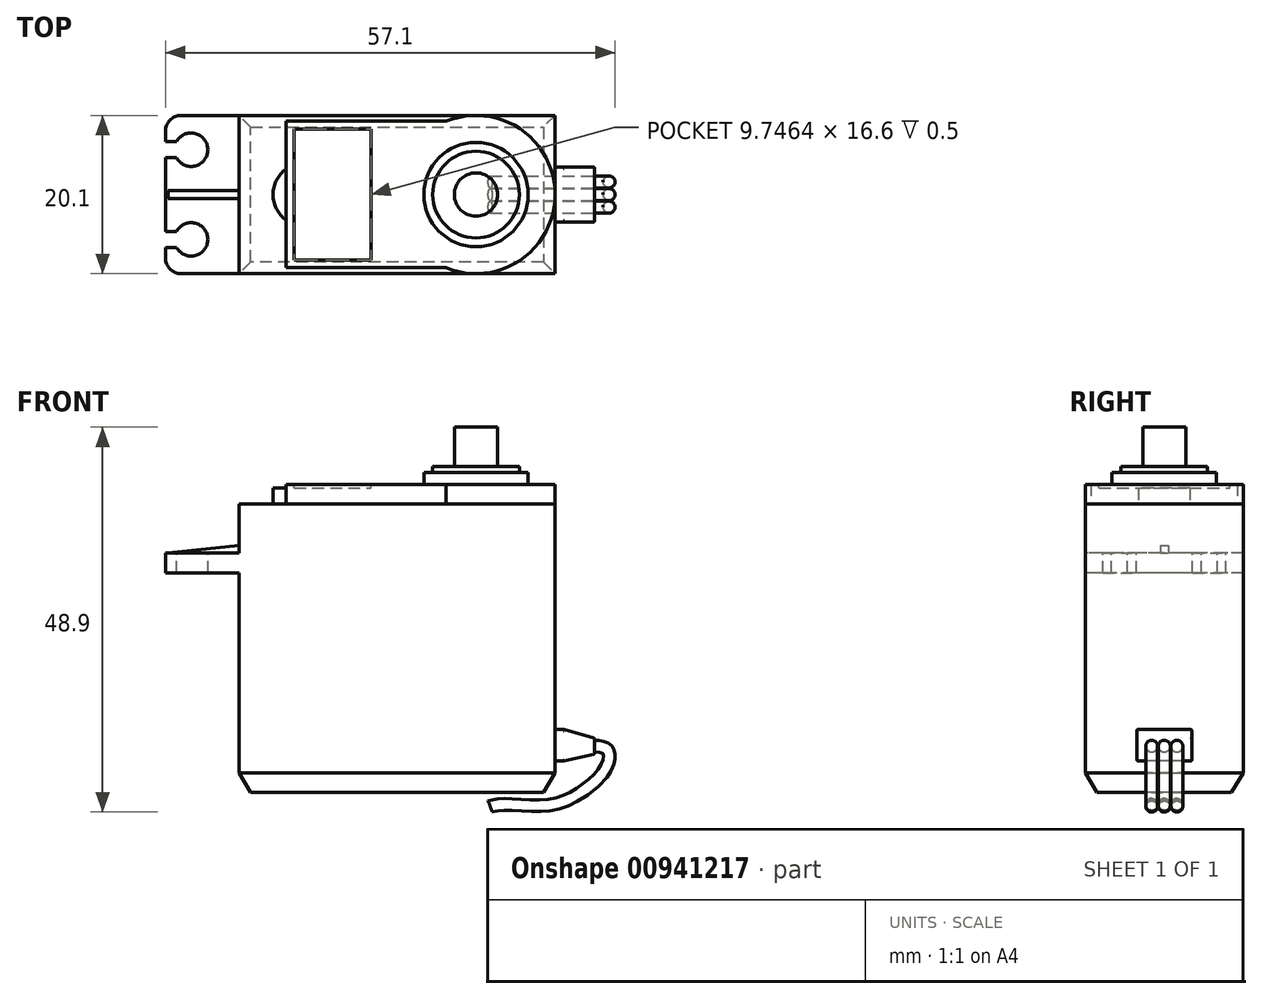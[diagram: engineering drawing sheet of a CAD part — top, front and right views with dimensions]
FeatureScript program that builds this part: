
annotation { "Feature Type Name" : "Feature", "Feature Type Description" : "" }
export const myFeature = defineFeature(function(context is Context, id is Id, definition is map)
    precondition{}
    {
        {
            var Q0;
            Q0=qCreatedBy(makeId("Front.planeOp"),FACE);
            var sketch = newSketch(context, id + "F0", { "sketchPlane" : qUnion([Q0])});
            skLineSegment(sketch, "E0.bottom", {"start": v(-20.07, 18.32) * mm, "end": v(20.08, 18.32) * mm});
            skLineSegment(sketch, "E0.top", {"start": v(-20.08, -18.32) * mm, "end": v(20.07, -18.32) * mm});
            skLineSegment(sketch, "E0.left", {"start": v(-20.07, 18.32) * mm, "end": v(-20.08, -18.32) * mm});
            skLineSegment(sketch, "E0.right", {"start": v(20.08, 18.32) * mm, "end": v(20.07, -18.32) * mm});
            skPoint(sketch, "E0.middle", {"position": v(0, 0) * mm});
            skSolve(sketch);
        }
        {
            var Q0;
            Q0 = qSketchRegion(id + "F0", true);
            extrude(context, id + "F1", {"entities" : qUnion([Q0]), "depth" : 20.1 * mm, "offsetDistance" : 25 * mm, "symmetric" : true});
        }
        {
            var Q0;
            Q0=makeQuery(id+"F1.opExtrude","CAP_EDGE",EDGE,{"disambiguationData":[OSD([sQuery(id+"F0.wireOp",EDGE,"E0.top")])],"isStart":false});
            var Q1;
            Q1=makeQuery(id+"F1.opExtrude","SWEPT_EDGE",EDGE,{"disambiguationData":[OSD([sQuery(id+"F0.wireOp",EDGE,"E0.top"),sQuery(id+"F0.wireOp",EDGE,"E0.right")])]});
            var Q2;
            Q2=makeQuery(id+"F1.opExtrude","CAP_EDGE",EDGE,{"disambiguationData":[OSD([sQuery(id+"F0.wireOp",EDGE,"E0.top")])],"isStart":true});
            var Q3;
            Q3=makeQuery(id+"F1.opExtrude","SWEPT_EDGE",EDGE,{"disambiguationData":[OSD([sQuery(id+"F0.wireOp",EDGE,"E0.top"),sQuery(id+"F0.wireOp",EDGE,"E0.left")])]});
            chamfer(context, id + "F2", {"entities" : qUnion([Q0, Q1, Q2, Q3]), "chamferType" : ChamferType.TWO_OFFSETS, "width1" : 2.5 * mm, "oppositeDirection" : false, "width2" : 1.5 * mm, "tangentPropagation" : true});
        }
        {
            var Q0;
            Q0=makeQuery(id+"F1.opExtrude","SWEPT_FACE",FACE,{"disambiguationData":[OSD([sQuery(id+"F0.wireOp",EDGE,"E0.bottom")])]});
            var sketch = newSketch(context, id + "F3", { "sketchPlane" : qUnion([Q0])});
            skArc(sketch, "E1", {"start": v(6.22, -9.3) * mm, "mid": v(20.08, 0) * mm, "end": v(6.22, 9.3) * mm});
            skPoint(sketch, "E1.first.point", {"position": v(20.08, 0) * mm});
            skPoint(sketch, "E1.second.point", {"position": v(10.03, -10.05) * mm});
            skPoint(sketch, "E1.third.point", {"position": v(10.03, 10.05) * mm});
            skLineSegment(sketch, "E2.2", {"start": v(-14.07, -9.3) * mm, "end": v(6.22, -9.3) * mm});
            skLineSegment(sketch, "E3.trimOffspring", {"start": v(6.22, 9.3) * mm, "end": v(-14.07, 9.3) * mm});
            skLineSegment(sketch, "E4", {"start": v(-14.07, -9.3) * mm, "end": v(-14.07, 9.3) * mm});
            skSolve(sketch);
        }
        {
            var Q0;
            Q0 = qSketchRegion(id + "F3", true);
            extrude(context, id + "F4", {"entities" : qUnion([Q0]), "operationType" : NewBodyOperationType.ADD, "depth" : 2.5 * mm, "offsetDistance" : 25 * mm});
        }
        {
            var Q0;
            {var subQ0=sQuery(id+"F0.wireOp",EDGE,"E0.left");var subQ1=sQuery(id+"F0.wireOp",EDGE,"E0.right");var subQ2=sQuery(id+"F0.wireOp",EDGE,"E0.top");var subQ3=sQuery(id+"F0.wireOp",EDGE,"E0.bottom");var subQ4=makeQuery(id+"F1.opExtrude","SWEPT_FACE",FACE,{"disambiguationData":[OSD([subQ3])]});Q0=makeQuery(id+"F4.boolean.opBoolean","SPLIT",FACE,{"disambiguationData":[TD([subQ4,makeQuery(id+"F1.opExtrude","CAP_FACE",FACE,{"disambiguationData":[OSD([subQ3,subQ2,subQ0,subQ1])],"isStart":true}),makeQuery(id+"F1.opExtrude","CAP_FACE",FACE,{"disambiguationData":[OSD([subQ3,subQ2,subQ0,subQ1])],"isStart":false}),makeQuery(id+"F1.opExtrude","SWEPT_FACE",FACE,{"disambiguationData":[OSD([subQ0])]}),makeQuery(id+"F4.opExtrude","SWEPT_FACE",FACE,{"disambiguationData":[OSD([sQuery(id+"F3.wireOp",EDGE,"E1")])]}),makeQuery(id+"F4.opExtrude","SWEPT_FACE",FACE,{"disambiguationData":[OSD([sQuery(id+"F3.wireOp",EDGE,"E2.2")])]}),makeQuery(id+"F4.opExtrude","SWEPT_FACE",FACE,{"disambiguationData":[OSD([sQuery(id+"F3.wireOp",EDGE,"E3.trimOffspring")])]}),makeQuery(id+"F4.opExtrude","SWEPT_FACE",FACE,{"disambiguationData":[OSD([sQuery(id+"F3.wireOp",EDGE,"E4")])]})])],"derivedFrom":subQ4});}
            var sketch = newSketch(context, id + "F5", { "sketchPlane" : qUnion([Q0])});
            skArc(sketch, "E5", {"start": v(-14.07, 3.26) * mm, "mid": v(-15.76, 0) * mm, "end": v(-14.07, -3.26) * mm});
            skLineSegment(sketch, "E6.0", {"start": v(-14.07, -3.26) * mm, "end": v(-14.07, 3.26) * mm});
            skPoint(sketch, "E7.orphan", {"position": v(-14.07, -9.3) * mm});
            skPoint(sketch, "E8.orphan", {"position": v(-14.07, 9.3) * mm});
            skSolve(sketch);
        }
        {
            var Q0;
            Q0 = qSketchRegion(id + "F5", true);
            extrude(context, id + "F6", {"entities" : qUnion([Q0]), "operationType" : NewBodyOperationType.ADD, "depth" : 2 * mm, "offsetDistance" : 25 * mm});
        }
        {
            var Q0;
            Q0=makeQuery(id+"F4.opExtrude","CAP_FACE",FACE,{"disambiguationData":[OSD([sQuery(id+"F3.wireOp",EDGE,"E1"),sQuery(id+"F3.wireOp",EDGE,"E2.2"),sQuery(id+"F3.wireOp",EDGE,"E3.trimOffspring"),sQuery(id+"F3.wireOp",EDGE,"E4")])],"isStart":false});
            var sketch = newSketch(context, id + "F7", { "sketchPlane" : qUnion([Q0])});
            skCircle(sketch, "E9", {"center": v(10.03, 0) * mm, "radius": 6.62 * mm});
            skSolve(sketch);
        }
        {
            var Q0;
            Q0 = qSketchRegion(id + "F7", true);
            extrude(context, id + "F8", {"entities" : qUnion([Q0]), "operationType" : NewBodyOperationType.ADD, "depth" : 1.5 * mm, "offsetDistance" : 25 * mm});
        }
        {
            var Q0;
            Q0=makeQuery(id+"F8.opExtrude","CAP_FACE",FACE,{"disambiguationData":[OSD([sQuery(id+"F7.wireOp",EDGE,"E9")])],"isStart":false});
            var sketch = newSketch(context, id + "F9", { "sketchPlane" : qUnion([Q0])});
            skCircle(sketch, "E10", {"center": v(10.03, 0) * mm, "radius": 5.5 * mm});
            skSolve(sketch);
        }
        {
            var Q0;
            Q0 = qSketchRegion(id + "F9", true);
            extrude(context, id + "F10", {"entities" : qUnion([Q0]), "operationType" : NewBodyOperationType.ADD, "depth" : 0.75 * mm, "offsetDistance" : 25 * mm});
        }
        {
            var Q0;
            Q0=makeQuery(id+"F10.opExtrude","CAP_FACE",FACE,{"disambiguationData":[OSD([sQuery(id+"F9.wireOp",EDGE,"E10")])],"isStart":false});
            var sketch = newSketch(context, id + "F11", { "sketchPlane" : qUnion([Q0])});
            skCircle(sketch, "E11", {"center": v(10.03, 0) * mm, "radius": 2.75 * mm});
            skSolve(sketch);
        }
        {
            var Q0;
            Q0 = qSketchRegion(id + "F11", true);
            extrude(context, id + "F12", {"entities" : qUnion([Q0]), "operationType" : NewBodyOperationType.ADD, "depth" : 5 * mm, "offsetDistance" : 25 * mm});
        }
        {
            var Q0;
            Q0=makeQuery(id+"F1.opExtrude","SWEPT_FACE",FACE,{"disambiguationData":[OSD([sQuery(id+"F0.wireOp",EDGE,"E0.right")])]});
            var sketch = newSketch(context, id + "F13", { "sketchPlane" : qUnion([Q0])});
            skLineSegment(sketch, "E12", {"start": v(0, -15.82) * mm, "end": v(0, -8.82) * mm, "construction": true});
            skLineSegment(sketch, "E13.bottom", {"start": v(3.31, -10.32) * mm, "end": v(-3.31, -10.32) * mm});
            skLineSegment(sketch, "E13.top", {"start": v(3.31, -14.32) * mm, "end": v(-3.31, -14.32) * mm});
            skLineSegment(sketch, "E13.left", {"start": v(3.5, -10.51) * mm, "end": v(3.5, -14.14) * mm});
            skLineSegment(sketch, "E13.right", {"start": v(-3.5, -10.51) * mm, "end": v(-3.5, -14.14) * mm});
            skPoint(sketch, "E13.middle", {"position": v(0, -12.32) * mm});
            skPoint(sketch, "E14.visualSharp", {"position": v(-3.5, -10.32) * mm});
            skArc(sketch, "E14.filletArc", {"start": v(-3.31, -10.32) * mm, "mid": v(-3.45, -10.38) * mm, "end": v(-3.5, -10.51) * mm});
            skPoint(sketch, "E15.visualSharp", {"position": v(-3.5, -14.32) * mm});
            skArc(sketch, "E15.filletArc", {"start": v(-3.5, -14.14) * mm, "mid": v(-3.45, -14.27) * mm, "end": v(-3.31, -14.32) * mm});
            skPoint(sketch, "E16.visualSharp", {"position": v(3.5, -10.32) * mm});
            skArc(sketch, "E16.filletArc", {"start": v(3.5, -10.51) * mm, "mid": v(3.45, -10.38) * mm, "end": v(3.31, -10.32) * mm});
            skPoint(sketch, "E17.visualSharp", {"position": v(3.5, -14.32) * mm});
            skArc(sketch, "E17.filletArc", {"start": v(3.31, -14.32) * mm, "mid": v(3.45, -14.27) * mm, "end": v(3.5, -14.14) * mm});
            skSolve(sketch);
        }
        {
            var Q0;
            Q0 = qSketchRegion(id + "F13", true);
            extrude(context, id + "F14", {"entities" : qUnion([Q0]), "operationType" : NewBodyOperationType.ADD, "depth" : 5 * mm, "offsetDistance" : 25 * mm});
        }
        {
            var Q0;
            Q0=makeQuery(id+"F14.opExtrude","SWEPT_FACE",FACE,{"disambiguationData":[OSD([sQuery(id+"F13.wireOp",EDGE,"E13.right")])]});
            var sketch = newSketch(context, id + "F15", { "sketchPlane" : qUnion([Q0])});
            skLineSegment(sketch, "E18", {"start": v(21.1, -14.34) * mm, "end": v(25.07, -13.5) * mm});
            skLineSegment(sketch, "E19", {"start": v(25.07, -11.41) * mm, "end": v(21.1, -10.3) * mm});
            skLineSegment(sketch, "E20", {"start": v(21.1, -10.3) * mm, "end": v(23.3, -9.11) * mm});
            skLineSegment(sketch, "E21", {"start": v(23.3, -9.11) * mm, "end": v(26.17, -9.55) * mm});
            skLineSegment(sketch, "E22", {"start": v(26.17, -9.55) * mm, "end": v(25.07, -11.41) * mm});
            skLineSegment(sketch, "E23", {"start": v(21.1, -14.34) * mm, "end": v(23.65, -15.38) * mm});
            skLineSegment(sketch, "E24", {"start": v(23.65, -15.38) * mm, "end": v(27.06, -14.85) * mm});
            skLineSegment(sketch, "E25", {"start": v(27.06, -14.85) * mm, "end": v(25.07, -13.5) * mm});
            skSolve(sketch);
        }
        {
            var Q0;
            Q0 = qSketchRegion(id + "F15", true);
            extrude(context, id + "F16", {"entities" : qUnion([Q0]), "operationType" : NewBodyOperationType.REMOVE, "oppositeDirection" : true, "depth" : 25 * mm, "offsetDistance" : 25 * mm});
        }
        {
            var Q0;
            Q0=makeQuery(id+"F16.boolean.opBoolean","COPY",FACE,{"derivedFrom":makeQuery(id+"F16.opExtrude","SWEPT_FACE",FACE,{"disambiguationData":[OSD([sQuery(id+"F15.wireOp",EDGE,"E19")])]})});
            var Q1;
            Q1=makeQuery(id+"F16.boolean.opBoolean","COPY",FACE,{"derivedFrom":makeQuery(id+"F16.opExtrude","SWEPT_FACE",FACE,{"disambiguationData":[OSD([sQuery(id+"F15.wireOp",EDGE,"E18")])]})});
            var Q2;
            Q2=makeQuery(id+"F14.opExtrude","CAP_FACE",FACE,{"disambiguationData":[OSD([sQuery(id+"F13.wireOp",EDGE,"E13.bottom"),sQuery(id+"F13.wireOp",EDGE,"E13.top"),sQuery(id+"F13.wireOp",EDGE,"E13.left"),sQuery(id+"F13.wireOp",EDGE,"E13.right"),sQuery(id+"F13.wireOp",EDGE,"E14.filletArc"),sQuery(id+"F13.wireOp",EDGE,"E15.filletArc"),sQuery(id+"F13.wireOp",EDGE,"E16.filletArc"),sQuery(id+"F13.wireOp",EDGE,"E17.filletArc")])],"isStart":false});
            fillet(context, id + "F17", {"entities" : qUnion([Q0, Q1, Q2]), "radius" : 0.18 * mm, "tangentPropagation" : true, "allowEdgeOverflow" : false});
        }
        {
            var Q0;
            Q0=makeQuery(id+"F1.opExtrude","CAP_FACE",FACE,{"disambiguationData":[OSD([sQuery(id+"F0.wireOp",EDGE,"E0.bottom"),sQuery(id+"F0.wireOp",EDGE,"E0.top"),sQuery(id+"F0.wireOp",EDGE,"E0.left"),sQuery(id+"F0.wireOp",EDGE,"E0.right")])],"isStart":false});
            var sketch = newSketch(context, id + "F18", { "sketchPlane" : qUnion([Q0])});
            skLineSegment(sketch, "E26.bottom", {"start": v(-20.07, 9.58) * mm, "end": v(-29.41, 9.58) * mm});
            skLineSegment(sketch, "E26.top", {"start": v(-20.07, 12.08) * mm, "end": v(-29.41, 12.08) * mm});
            skLineSegment(sketch, "E26.left", {"start": v(-20.07, 9.58) * mm, "end": v(-20.07, 12.08) * mm});
            skLineSegment(sketch, "E26.right", {"start": v(-29.41, 9.58) * mm, "end": v(-29.41, 12.08) * mm});
            skSolve(sketch);
        }
        {
            var Q0;
            Q0 = qSketchRegion(id + "F18", true);
            var Q1;
            Q1=makeQuery(id+"F1.opExtrude","CAP_FACE",FACE,{"disambiguationData":[OSD([sQuery(id+"F0.wireOp",EDGE,"E0.bottom"),sQuery(id+"F0.wireOp",EDGE,"E0.top"),sQuery(id+"F0.wireOp",EDGE,"E0.left"),sQuery(id+"F0.wireOp",EDGE,"E0.right")])],"isStart":true});
            extrude(context, id + "F19", {"entities" : qUnion([Q0]), "operationType" : NewBodyOperationType.ADD, "endBound" : BoundingType.UP_TO_SURFACE, "oppositeDirection" : true, "depth" : 25 * mm, "endBoundEntityFace" : qUnion([Q1]), "offsetDistance" : 25 * mm});
        }
        {
            var Q0;
            Q0=makeQuery(id+"F19.opExtrude","SWEPT_FACE",FACE,{"disambiguationData":[OSD([sQuery(id+"F18.wireOp",EDGE,"E26.top")])]});
            var sketch = newSketch(context, id + "F20", { "sketchPlane" : qUnion([Q0])});
            skArc(sketch, "E27", {"start": v(-28.03, 4.68) * mm, "mid": v(-24.04, 5.7) * mm, "end": v(-28.03, 6.72) * mm});
            skLineSegment(sketch, "E28.0", {"start": v(-27.41, 10.05) * mm, "end": v(-20.07, 10.05) * mm});
            skLineSegment(sketch, "E29.0", {"start": v(-29.41, 8.05) * mm, "end": v(-29.41, -8.05) * mm});
            skLineSegment(sketch, "E30.0", {"start": v(-20.07, -10.05) * mm, "end": v(-27.41, -10.05) * mm});
            skPoint(sketch, "E31.visualSharp", {"position": v(-29.41, 10.05) * mm});
            skArc(sketch, "E31.filletArc", {"start": v(-27.41, 10.05) * mm, "mid": v(-28.83, 9.46) * mm, "end": v(-29.41, 8.05) * mm});
            skPoint(sketch, "E32.visualSharp", {"position": v(-29.41, -10.05) * mm});
            skArc(sketch, "E32.filletArc", {"start": v(-29.41, -8.05) * mm, "mid": v(-28.83, -9.46) * mm, "end": v(-27.41, -10.05) * mm});
            skPoint(sketch, "E33.0.end.orphan", {"position": v(-20.07, 10.05) * mm});
            skPoint(sketch, "E33.0.start.orphan", {"position": v(-20.07, -10.05) * mm});
            skLineSegment(sketch, "E34.bottom", {"start": v(-30.55, 6.72) * mm, "end": v(-28.03, 6.72) * mm});
            skLineSegment(sketch, "E34.top", {"start": v(-30.55, 4.68) * mm, "end": v(-28.03, 4.68) * mm});
            skLineSegment(sketch, "E34.left", {"start": v(-30.55, 6.72) * mm, "end": v(-30.55, 4.68) * mm});
            skLineSegment(sketch, "E35.MirrorCS", {"start": v(-30.55, -6.72) * mm, "end": v(-28.03, -6.72) * mm});
            skLineSegment(sketch, "E36.MirrorCS", {"start": v(-30.55, -6.72) * mm, "end": v(-30.55, -4.68) * mm});
            skLineSegment(sketch, "E37.MirrorCS", {"start": v(-30.55, -4.68) * mm, "end": v(-28.03, -4.68) * mm});
            skArc(sketch, "E38.MirrorCS", {"start": v(-28.03, -4.68) * mm, "mid": v(-24.04, -5.7) * mm, "end": v(-28.03, -6.72) * mm});
            skLineSegment(sketch, "E39", {"start": v(-20.07, 10.05) * mm, "end": v(-20.07, 11.68) * mm});
            skLineSegment(sketch, "E40", {"start": v(-20.07, 11.68) * mm, "end": v(-36.52, 11.68) * mm});
            skLineSegment(sketch, "E41", {"start": v(-36.52, 11.68) * mm, "end": v(-36.52, -10.64) * mm});
            skLineSegment(sketch, "E42", {"start": v(-36.52, -10.64) * mm, "end": v(-20.07, -10.64) * mm});
            skLineSegment(sketch, "E43", {"start": v(-20.07, -10.64) * mm, "end": v(-20.07, -10.05) * mm});
            skSolve(sketch);
        }
        {
            var Q0;
            Q0 = qSketchRegion(id + "F20", true);
            extrude(context, id + "F21", {"entities" : qUnion([Q0]), "operationType" : NewBodyOperationType.REMOVE, "oppositeDirection" : true, "depth" : 25 * mm, "offsetDistance" : 25 * mm});
        }
        {
            var Q0;
            Q0=makeQuery(id+"F14.opExtrude","CAP_FACE",FACE,{"disambiguationData":[OSD([sQuery(id+"F13.wireOp",EDGE,"E13.bottom"),sQuery(id+"F13.wireOp",EDGE,"E13.top"),sQuery(id+"F13.wireOp",EDGE,"E13.left"),sQuery(id+"F13.wireOp",EDGE,"E13.right"),sQuery(id+"F13.wireOp",EDGE,"E14.filletArc"),sQuery(id+"F13.wireOp",EDGE,"E15.filletArc"),sQuery(id+"F13.wireOp",EDGE,"E16.filletArc"),sQuery(id+"F13.wireOp",EDGE,"E17.filletArc")])],"isStart":false});
            var sketch = newSketch(context, id + "F22", { "sketchPlane" : qUnion([Q0])});
            skCircle(sketch, "E44", {"center": v(0, -12.45) * mm, "radius": 0.75 * mm});
            skPoint(sketch, "E44.centerSnap0", {"position": v(-3.32, -12.45) * mm});
            skPoint(sketch, "E44.centerSnap1", {"position": v(0, -11.55) * mm});
            skCircle(sketch, "E45", {"center": v(-1.6, -12.45) * mm, "radius": 0.75 * mm});
            skCircle(sketch, "E46", {"center": v(1.6, -12.45) * mm, "radius": 0.75 * mm});
            skSolve(sketch);
        }
        {
            var Q0;
            Q0=qCreatedBy(makeId("Front.planeOp"),FACE);
            var sketch = newSketch(context, id + "F23", { "sketchPlane" : qUnion([Q0])});
            skFitSpline(sketch, "E47", {"points": [v(25.07, -12.45) * mm, v(26.68, -12.87) * mm, v(26.68, -14.94) * mm, v(23.89, -17.95) * mm, v(19.3, -19.93) * mm, v(13.53, -19.83) * mm, v(11.84, -20.12) * mm], "startDerivative": vector(15.64, -1.15) * mm, "endDerivative": vector(-11.38, -3.28) * mm});
            skSolve(sketch);
        }
        {
            var Q0;
            Q0=makeQuery(id+"F22.imprint","IMPRINT",FACE,{"disambiguationData":[TD([[makeQuery(id+"F22.imprint","IMPRINT",EDGE,{"derivedFrom":sQuery(id+"F22.wireOp",EDGE,"E44")}),1.0]])]});
            var Q1;
            Q1=makeQuery(id+"F22.imprint","IMPRINT",FACE,{"disambiguationData":[TD([[makeQuery(id+"F22.imprint","IMPRINT",EDGE,{"derivedFrom":sQuery(id+"F22.wireOp",EDGE,"E45")}),1.0]])]});
            var Q2;
            Q2=makeQuery(id+"F22.imprint","IMPRINT",FACE,{"disambiguationData":[TD([[makeQuery(id+"F22.imprint","IMPRINT",EDGE,{"derivedFrom":sQuery(id+"F22.wireOp",EDGE,"E46")}),1.0]])]});
            var Q3;
            Q3=sQuery(id+"F23.wireOp",EDGE,"E47");
            sweep(context, id + "F24", {"operationType" : NewBodyOperationType.ADD, "profiles" : qUnion([Q0, Q1, Q2]), "path" : qUnion([Q3])});
        }
        {
            var Q0;
            Q0=qCreatedBy(makeId("Front.planeOp"),FACE);
            var sketch = newSketch(context, id + "F25", { "sketchPlane" : qUnion([Q0])});
            skLineSegment(sketch, "E48.0", {"start": v(-20.07, 13.07) * mm, "end": v(-20.07, 12.08) * mm});
            skLineSegment(sketch, "E49", {"start": v(-20.07, 12.08) * mm, "end": v(-29.07, 12.08) * mm});
            skLineSegment(sketch, "E50", {"start": v(-29.07, 12.08) * mm, "end": v(-20.07, 13.07) * mm});
            skPoint(sketch, "E51.orphan", {"position": v(-20.07, 18.32) * mm});
            skSolve(sketch);
        }
        {
            var Q0;
            Q0 = qSketchRegion(id + "F25", true);
            extrude(context, id + "F26", {"entities" : qUnion([Q0]), "operationType" : NewBodyOperationType.ADD, "depth" : 1 * mm, "offsetDistance" : 25 * mm, "symmetric" : true});
        }
        {
            var Q0;
            Q0=makeQuery(id+"F4.opExtrude","CAP_FACE",FACE,{"disambiguationData":[OSD([sQuery(id+"F3.wireOp",EDGE,"E1"),sQuery(id+"F3.wireOp",EDGE,"E2.2"),sQuery(id+"F3.wireOp",EDGE,"E3.trimOffspring"),sQuery(id+"F3.wireOp",EDGE,"E4")])],"isStart":false});
            var sketch = newSketch(context, id + "F27", { "sketchPlane" : qUnion([Q0])});
            skLineSegment(sketch, "E52.0", {"start": v(-13.07, 8.3) * mm, "end": v(-13.07, -8.3) * mm});
            skLineSegment(sketch, "E52.1", {"start": v(-3.33, 8.3) * mm, "end": v(-13.07, 8.3) * mm});
            skLineSegment(sketch, "E52.3", {"start": v(-13.07, -8.3) * mm, "end": v(-3.33, -8.3) * mm});
            skLineSegment(sketch, "E53", {"start": v(-3.33, 8.3) * mm, "end": v(-3.33, -8.3) * mm});
            skSolve(sketch);
        }
        {
            var Q0;
            Q0 = qSketchRegion(id + "F27", true);
            var Q1;
            Q1=makeQuery(id+"F6.opExtrude","CAP_FACE",FACE,{"disambiguationData":[OSD([sQuery(id+"F5.wireOp",EDGE,"E5"),sQuery(id+"F5.wireOp",EDGE,"E6.0")])],"isStart":false});
            extrude(context, id + "F28", {"entities" : qUnion([Q0]), "operationType" : NewBodyOperationType.REMOVE, "endBound" : BoundingType.UP_TO_SURFACE, "oppositeDirection" : true, "depth" : 25 * mm, "endBoundEntityFace" : qUnion([Q1]), "offsetDistance" : 25 * mm});
        }
    });
